# Revit family: BoelsRental_TelescopicBoomLift_Genie_SX125XCa
name_source: partatom
category: Site
units: mm (PartAtom-declared; Revit-internal decimal feet)

## family parameters
Always vertical = Yes
Cut with Voids When Loaded = No
OmniClass Number = 23.50.85.17
OmniClass Title = Telescoping Platforms
Part Type = Normal
Round Connector Dimension = Use Diameter
Shared = No
Work Plane-Based = No

## types (1)
- SX125XC
    Assembly Code = E1030100
    AssetType = Movable
    BIMObjectName = BoelsRental_TelescopicBoomLift_Genie_SX125XC
    BoelsSubgroup = 18031 - Telescopic boom lift 40 m
    ClassificationName = Uniclass2015
    ClassificationValue = Pr_65_80_47_95
    Cost = 0 $
    Description = TELESCOPIC BOOM LIFT, DIESEL < 40 M CAPACITY >300KG
    DocumentationCertificates = https://www.boels.com
    DocumentationInstallationGuide = https://www.boels.com
    DocumentationLiterature = https://www.boels.com
    DocumentationMaintenance = https://www.boels.com
    DocumentationTechnical = https://www.boels.com
    DurationUnit = Years
    ExpectedLife = 0
    IfcExportAs = IfcTransportElement
    IfcExportType = IfcTransportElementType
    Keynote = X
    Manufacturer = Boels Rental (Genie)
    ManufacturerName = Boels Rental (Genie)
    Material = Steel
    Model = Telescopic Boom Lift - SX125XC
    ModelNumber = SX125XC
    ModelReference = Telescopic Boom Lift
    NBSDescription = Vertical lifting platforms
    NBSObjectName = Boels Rental - Vertical lifting platforms
    NBSReference = 90-80-65/350
    NominalDepth = 2490 mm
    NominalHeight = 3050 mm
    NominalLength = 14250 mm
    ProductPageLink = https://www.boels.com
    ProductionYear = 2022
    Size = 2.49m x 3.05m x 14.25m
    Type Comments = Telescopic Boom Lift - SX125XC
    TypeName = Telescopic Boom Lift - SX125XC
    URL = https://www.boels.com
    WarrantyDurationLabor = 0
    WarrantyDurationParts = 0
    WarrantyDurationUnit = Years
    WarrantyGuarantorLabor = https://www.boels.com
    WarrantyGuarantorParts = https://www.boels.com
    _BSBibleVersion = 16
    _BimSpecGuid = 0
    _CurrentRevision = 1
    _DistributedBy = https://www.boels.com
    _ObjectUserGuide = https://www.boels.com

## geometry (parser evidence)
native form markers: Sweep x39
no freeform markers — native parametric forms only
